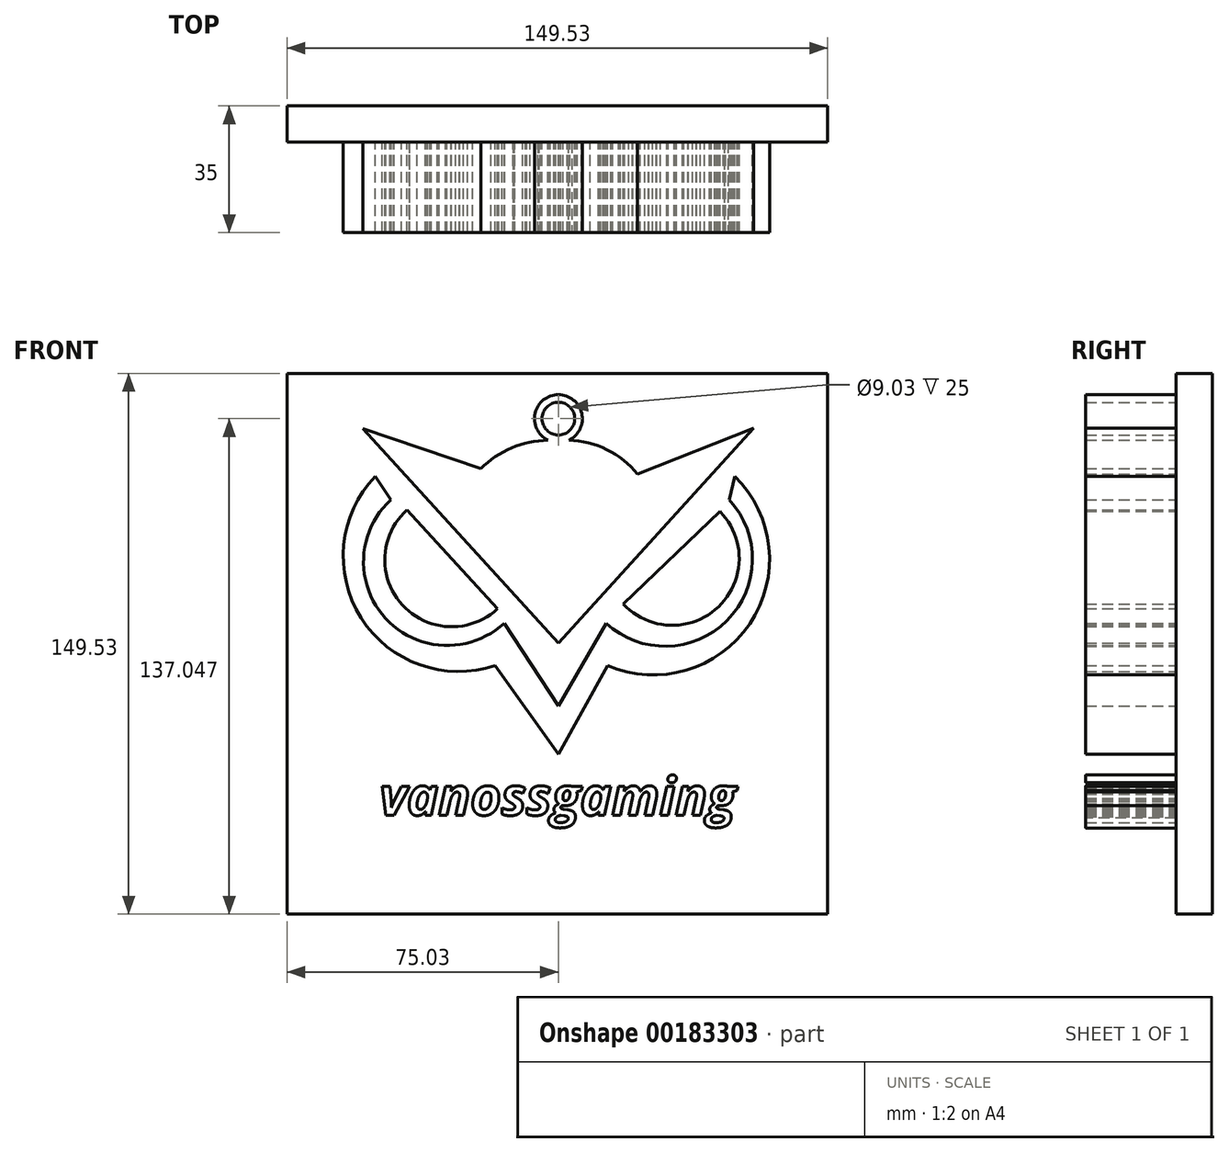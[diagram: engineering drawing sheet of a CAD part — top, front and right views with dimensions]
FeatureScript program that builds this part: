
annotation { "Feature Type Name" : "Feature", "Feature Type Description" : "" }
export const myFeature = defineFeature(function(context is Context, id is Id, definition is map)
    precondition{}
    {
        {
            var Q0;
            Q0=qCreatedBy(makeId("Front.planeOp"),FACE);
            var sketch = newSketch(context, id + "F0", { "sketchPlane" : qUnion([Q0])});
            skLineSegment(sketch, "E0", {"start": v(-54.1, 59.23) * mm, "end": v(0, 0) * mm});
            skLineSegment(sketch, "E1", {"start": v(0, 0) * mm, "end": v(53.97, 59.35) * mm});
            skLineSegment(sketch, "E2", {"start": v(-54.1, 59.23) * mm, "end": v(-21.45, 48.17) * mm});
            skLineSegment(sketch, "E3", {"start": v(53.97, 59.35) * mm, "end": v(21.9, 46.68) * mm});
            skArc(sketch, "E4", {"start": v(21.9, 46.68) * mm, "mid": v(12.1, 54.04) * mm, "end": v(0, 56) * mm});
            skArc(sketch, "E5", {"start": v(0, 56) * mm, "mid": v(-11.58, 54.42) * mm, "end": v(-21.45, 48.17) * mm});
            skSolve(sketch);
        }
        {
            var Q0;
            Q0 = qSketchRegion(id + "F0", true);
            extrude(context, id + "F1", {"entities" : qUnion([Q0]), "depth" : 25 * mm});
        }
        {
            var Q0;
            Q0=qCreatedBy(makeId("Front.planeOp"),FACE);
            var sketch = newSketch(context, id + "F2", { "sketchPlane" : qUnion([Q0])});
            skLineSegment(sketch, "E6", {"start": v(-41.83, 36.79) * mm, "end": v(-16.86, 9.43) * mm});
            skArc(sketch, "E7", {"start": v(-41.83, 36.79) * mm, "mid": v(-43.16, 10.5) * mm, "end": v(-16.86, 9.43) * mm});
            skLineSegment(sketch, "E8", {"start": v(-53.52, 59.1) * mm, "end": v(-41.83, 36.79) * mm});
            skLineSegment(sketch, "E9", {"start": v(54.05, 59.1) * mm, "end": v(44.7, 36.36) * mm});
            skLineSegment(sketch, "E10", {"start": v(44.7, 36.36) * mm, "end": v(17.93, 10.75) * mm});
            skArc(sketch, "E11", {"start": v(17.93, 10.75) * mm, "mid": v(44.3, 9.99) * mm, "end": v(44.7, 36.36) * mm});
            skSolve(sketch);
        }
        {
            var Q0;
            Q0 = qSketchRegion(id + "F2", true);
            extrude(context, id + "F3", {"entities" : qUnion([Q0]), "depth" : 25 * mm});
        }
        {
            var Q0;
            Q0=qCreatedBy(makeId("Front.planeOp"),FACE);
            var sketch = newSketch(context, id + "F4", { "sketchPlane" : qUnion([Q0])});
            skCircle(sketch, "E12", {"center": v(0, 62.02) * mm, "radius": 6.61 * mm});
            skSolve(sketch);
        }
        {
            var Q0;
            Q0 = qSketchRegion(id + "F4", true);
            extrude(context, id + "F5", {"entities" : qUnion([Q0]), "operationType" : NewBodyOperationType.ADD, "depth" : 25 * mm});
        }
        {
            var Q0;
            Q0=qCreatedBy(makeId("Front.planeOp"),FACE);
            var sketch = newSketch(context, id + "F6", { "sketchPlane" : qUnion([Q0])});
            skCircle(sketch, "E13", {"center": v(0, 62.02) * mm, "radius": 4.52 * mm});
            skSolve(sketch);
        }
        {
            var Q0;
            Q0 = qSketchRegion(id + "F6", true);
            extrude(context, id + "F7", {"entities" : qUnion([Q0]), "operationType" : NewBodyOperationType.REMOVE, "depth" : 25.3 * mm});
        }
        {
            var Q0;
            Q0=qCreatedBy(makeId("Front.planeOp"),FACE);
            var sketch = newSketch(context, id + "F8", { "sketchPlane" : qUnion([Q0])});
            skLineSegment(sketch, "E14.bottom", {"start": v(-75.03, 74.5) * mm, "end": v(74.5, 74.5) * mm});
            skLineSegment(sketch, "E14.top", {"start": v(-75.03, -75.03) * mm, "end": v(74.5, -75.03) * mm});
            skLineSegment(sketch, "E14.left", {"start": v(-75.03, 74.5) * mm, "end": v(-75.03, -75.03) * mm});
            skLineSegment(sketch, "E14.right", {"start": v(74.5, 74.5) * mm, "end": v(74.5, -75.03) * mm});
            skSolve(sketch);
        }
        {
            var Q0;
            Q0 = qSketchRegion(id + "F8", true);
            extrude(context, id + "F9", {"entities" : qUnion([Q0]), "oppositeDirection" : true, "depth" : 10 * mm});
        }
        {
            var Q0;
            Q0=makeQuery(id+"F9.opExtrude","CAP_FACE",FACE,{"disambiguationData":[OSD([sQuery(id+"F8.wireOp",EDGE,"E14.bottom"),sQuery(id+"F8.wireOp",EDGE,"E14.top"),sQuery(id+"F8.wireOp",EDGE,"E14.left"),sQuery(id+"F8.wireOp",EDGE,"E14.right")])],"isStart":true});
            var sketch = newSketch(context, id + "F10", { "sketchPlane" : qUnion([Q0])});
            skLineSegment(sketch, "E15", {"start": v(-46.37, 39.54) * mm, "end": v(-50.62, 46.08) * mm});
            skArc(sketch, "E16", {"start": v(-46.37, 39.54) * mm, "mid": v(-47.79, 6.77) * mm, "end": v(-15.03, 5.43) * mm});
            skArc(sketch, "E17", {"start": v(-50.62, 46.08) * mm, "mid": v(-54.57, 6.93) * mm, "end": v(-17.49, -6.22) * mm});
            skLineSegment(sketch, "E18", {"start": v(-15.03, 5.43) * mm, "end": v(0, -17.39) * mm});
            skLineSegment(sketch, "E19", {"start": v(0, -17.39) * mm, "end": v(13.2, 5.43) * mm});
            skLineSegment(sketch, "E20", {"start": v(-17.49, -6.22) * mm, "end": v(0, -30.73) * mm});
            skLineSegment(sketch, "E21", {"start": v(0, -30.73) * mm, "end": v(13.6, -6.22) * mm});
            skLineSegment(sketch, "E22", {"start": v(47.29, 39.54) * mm, "end": v(48.8, 46.08) * mm});
            skArc(sketch, "E23", {"start": v(13.6, -6.22) * mm, "mid": v(52.95, 5.3) * mm, "end": v(48.8, 46.08) * mm});
            skArc(sketch, "E24", {"start": v(13.2, 5.43) * mm, "mid": v(46.6, 6.13) * mm, "end": v(47.29, 39.54) * mm});
            skSolve(sketch);
        }
        {
            var Q0;
            Q0=makeQuery(id+"F10.imprint","IMPRINT",FACE,{"disambiguationData":[TD([[makeQuery(id+"F10.imprint","IMPRINT",EDGE,{"derivedFrom":sQuery(id+"F10.wireOp",EDGE,"E15")}),1.0]])]});
            extrude(context, id + "F11", {"entities" : qUnion([Q0]), "operationType" : NewBodyOperationType.ADD, "depth" : 25 * mm});
        }
        {
            var Q0;
            Q0=makeQuery(id+"F1.opExtrude","SWEPT_BODY",BODY,{"disambiguationData":[OSD([sQuery(id+"F0.wireOp",EDGE,"E0"),sQuery(id+"F0.wireOp",EDGE,"E1"),sQuery(id+"F0.wireOp",EDGE,"E2"),sQuery(id+"F0.wireOp",EDGE,"E3"),sQuery(id+"F0.wireOp",EDGE,"E4"),sQuery(id+"F0.wireOp",EDGE,"E5")])]});
            var Q1;
            Q1=makeQuery(id+"F3.opExtrude","SWEPT_BODY",BODY,{"disambiguationData":[OSD([sQuery(id+"F2.wireOp",EDGE,"E6"),sQuery(id+"F2.wireOp",EDGE,"E7")])]});
            var Q2;
            Q2=makeQuery(id+"F3.opExtrude","SWEPT_BODY",BODY,{"disambiguationData":[OSD([sQuery(id+"F2.wireOp",EDGE,"E10"),sQuery(id+"F2.wireOp",EDGE,"E11")])]});
            var Q3;
            Q3=makeQuery(id+"F9.opExtrude","SWEPT_BODY",BODY,{"disambiguationData":[OSD([sQuery(id+"F8.wireOp",EDGE,"E14.bottom"),sQuery(id+"F8.wireOp",EDGE,"E14.top"),sQuery(id+"F8.wireOp",EDGE,"E14.left"),sQuery(id+"F8.wireOp",EDGE,"E14.right")])]});
            booleanBodies(context, id + "F12", {"operationType" : BooleanOperationType.UNION, "tools" : qUnion([Q0, Q1, Q2, Q3])});
        }
        {
            var Q0;
            {var subQ0=sQuery(id+"F8.wireOp",EDGE,"E14.top");var subQ1=sQuery(id+"F8.wireOp",EDGE,"E14.right");var subQ2=sQuery(id+"F8.wireOp",EDGE,"E14.bottom");var subQ3=sQuery(id+"F8.wireOp",EDGE,"E14.left");Q0=makeQuery(id+"F12.opBoolean","SPLIT",FACE,{"disambiguationData":[TD([makeQuery(id+"F1.opExtrude","SWEPT_FACE",FACE,{"disambiguationData":[OSD([sQuery(id+"F0.wireOp",EDGE,"E0")])]})])],"derivedFrom":makeQuery(id+"F9.opExtrude","CAP_FACE",FACE,{"disambiguationData":[OSD([subQ2,subQ0,subQ3,subQ1])],"isStart":true})});}
            var sketch = newSketch(context, id + "F13", { "sketchPlane" : qUnion([Q0])});
            skText(sketch, "E25", { "text": "vanossgaming\n", "fontName": "OpenSans-BoldItalic.ttf"});
            const initialGuessF13  = {"E25": [-0.04942, -0.04765, 1, 0, 0.01055]};
            skSetInitialGuess(sketch, initialGuessF13);
            skSolve(sketch);
        }
        {
            var Q0;
            Q0 = qSketchRegion(id + "F13", true);
            extrude(context, id + "F14", {"entities" : qUnion([Q0]), "operationType" : NewBodyOperationType.ADD, "depth" : 25 * mm});
        }
    });
